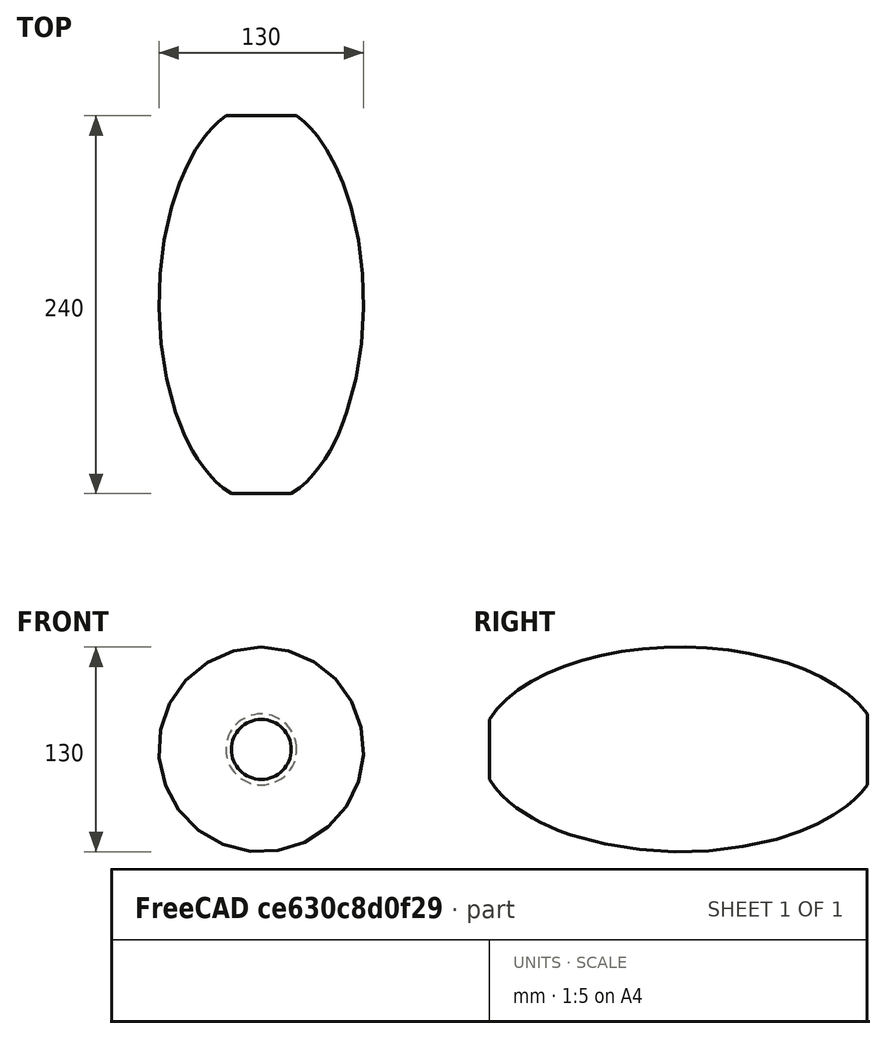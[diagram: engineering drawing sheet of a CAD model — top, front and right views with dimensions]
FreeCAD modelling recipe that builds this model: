
FCSTD DOCUMENT  (FreeCAD 0.18R4 (GitTag))
Label: Ambu
License: All rights reserved
LicenseURL: http://en.wikipedia.org/wiki/All_rights_reserved
objects: Sketcher::SketchObject×1, PartDesign::Revolution×1, PartDesign::Body×1
note: 4 computed .brp shape members not serialized (recipe doc carries the construction recipe); baked Part::Feature solids carry a one-line shape summary decoded from their .brp

FEATURE [Sketcher::SketchObject] Sketch
  MapMode = 5
  Placement = pos=(0,0,0) rot=(0.57735,0.57735,0.57735;2.0944rad)
  Support = -> [YZ_Plane]
  sketch-geometry (8):
    g0: LineSegment StartX=-1.42e-14 StartY=0 StartZ=0 EndX=-1.42e-14 EndY=19 EndZ=0
    g1: LineSegment StartX=-1.42e-14 StartY=0 StartZ=0 EndX=240 EndY=0 EndZ=0
    g2: LineSegment StartX=240 StartY=0 StartZ=0 EndX=240 EndY=22.5 EndZ=0
    g3: ArcOfEllipse CenterX=121.149 CenterY=0 CenterZ=0 NormalX=0 NormalY=0 NormalZ=1 MajorRadius=126.682 MinorRadius=65 AngleXU=1e-16 StartAngle=0.353468 EndAngle=2.84495
    g4: LineSegment [constr] StartX=247.832 StartY=1.35e-14 StartZ=0 EndX=-5.53294 EndY=-1.35e-14 EndZ=0
    g5: LineSegment [constr] StartX=121.149 StartY=65 StartZ=0 EndX=121.149 EndY=-65 EndZ=0
    g6: GeomPoint X=229.885 Y=1.16e-14 Z=0
    g7: GeomPoint X=12.4139 Y=-1.16e-14 Z=0
  constraints (15):
    c: Horizontal(g1)
    c: Vertical(g2)
    c: Vertical(g0)
    c: DistanceX(g1,g1) = 240
    c: Coincident(g1,g0)
    c: Coincident(g1,g-1)
    c: Coincident(g1,g2)
    c: DistanceY(g2,g2) = 22.5
    c: DistanceY(g0,g0) = 19
    c: InternalAlignment(g4-g7 -> g3) x4
    c: Vertical(g5)
    c: DistanceY(g5,g5) = 130
    c: PointOnObject(g3,g1)
    c: Coincident(g0,g3)
    c: Coincident(g2,g3)
FEATURE [PartDesign::Revolution] Revolution
  Angle = 360
  Axis = (3e-16,1,-2e-16)
  Base = (0,0,0)
  Placement = pos=(0,0,0) rot=(0.57735,0.57735,0.57735;2.0944rad)
  Profile = -> Sketch
  ReferenceAxis = -> Sketch [H_Axis]
FEATURE [PartDesign::Body] Body
  Group = -> [Sketch,Revolution]
  Origin = -> Origin
  Tip = -> Revolution
